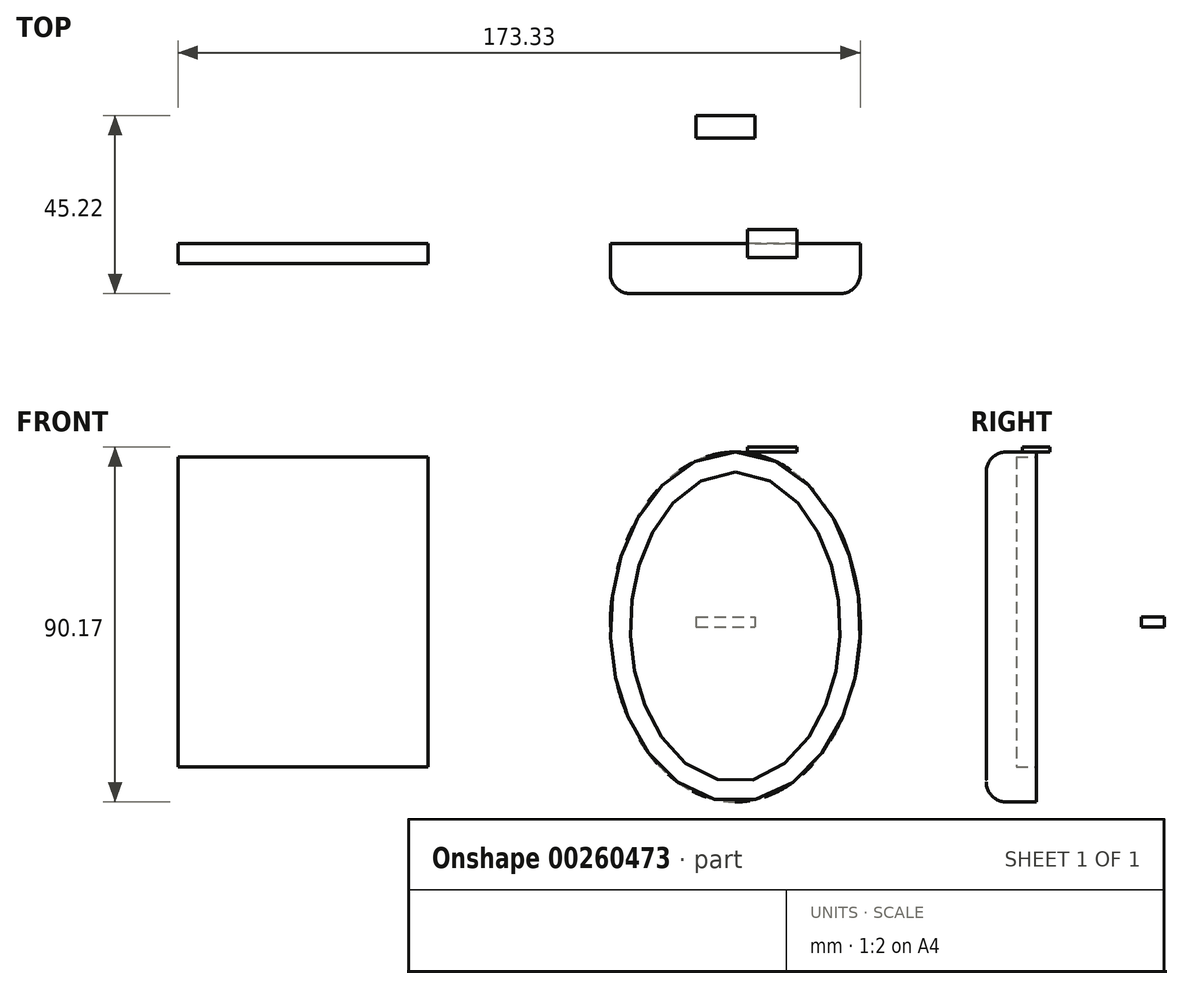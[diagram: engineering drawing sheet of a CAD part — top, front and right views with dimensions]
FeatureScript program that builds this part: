
annotation { "Feature Type Name" : "Feature", "Feature Type Description" : "" }
export const myFeature = defineFeature(function(context is Context, id is Id, definition is map)
    precondition{}
    {
        {
            var Q0;
            Q0=qCreatedBy(makeId("Front.planeOp"),FACE);
            var sketch = newSketch(context, id + "F0", { "sketchPlane" : qUnion([Q0])});
            skEllipse(sketch, "E0", {"center": v(0, 0) * mm, "majorRadius": 31.75 * mm, "minorRadius": 44.45 * mm, "majorAxis": v(1, 0)});
            skSolve(sketch);
        }
        {
            var Q0;
            Q0=makeQuery(id+"F0.imprint","IMPRINT",FACE,{"disambiguationData":[TD([[makeQuery(id+"F0.imprint","IMPRINT",EDGE,{"derivedFrom":sQuery(id+"F0.wireOp",EDGE,"E0")}),1.0]])]});
            extrude(context, id + "F1", {"entities" : qUnion([Q0]), "depth" : 12.7 * mm});
        }
        {
            var Q0;
            Q0=makeQuery(id+"F1.opExtrude","CAP_FACE",FACE,{"disambiguationData":[OSD([sQuery(id+"F0.wireOp",EDGE,"E0")])],"isStart":false});
            fillet(context, id + "F2", {"entities" : qUnion([Q0]), "radius" : 5.08 * mm, "tangentPropagation" : true, "allowEdgeOverflow" : false});
        }
        {
            var Q0;
            Q0=qCreatedBy(makeId("Front.planeOp"),FACE);
            var sketch = newSketch(context, id + "F3", { "sketchPlane" : qUnion([Q0])});
            skLineSegment(sketch, "E1.bottom", {"start": v(-141.58, 43.19) * mm, "end": v(-78.08, 43.19) * mm});
            skLineSegment(sketch, "E1.top", {"start": v(-141.58, -35.55) * mm, "end": v(-78.08, -35.55) * mm});
            skLineSegment(sketch, "E1.left", {"start": v(-141.58, 43.19) * mm, "end": v(-141.58, -35.55) * mm});
            skLineSegment(sketch, "E1.right", {"start": v(-78.08, 43.19) * mm, "end": v(-78.08, -35.55) * mm});
            skPoint(sketch, "E1.middle", {"position": v(-109.83, 3.82) * mm});
            skSolve(sketch);
        }
        {
            var Q0;
            Q0=makeQuery(id+"F3.imprint","IMPRINT",FACE,{"disambiguationData":[TD([[makeQuery(id+"F3.imprint","IMPRINT",EDGE,{"derivedFrom":sQuery(id+"F3.wireOp",EDGE,"E1.bottom")}),-1.0]])]});
            extrude(context, id + "F4", {"entities" : qUnion([Q0]), "depth" : 5.08 * mm});
        }
        {
            var Q0;
            Q0=qCreatedBy(makeId("Top.planeOp"),FACE);
            var sketch = newSketch(context, id + "F5", { "sketchPlane" : qUnion([Q0])});
            skLineSegment(sketch, "E2.bottom", {"start": v(-9.93, 32.52) * mm, "end": v(4.97, 32.52) * mm});
            skLineSegment(sketch, "E2.top", {"start": v(-9.93, 26.74) * mm, "end": v(4.97, 26.74) * mm});
            skLineSegment(sketch, "E2.left", {"start": v(-9.93, 32.52) * mm, "end": v(-9.93, 26.74) * mm});
            skLineSegment(sketch, "E2.right", {"start": v(4.97, 32.52) * mm, "end": v(4.97, 26.74) * mm});
            skSolve(sketch);
        }
        {
            var Q0;
            Q0=makeQuery(id+"F5.imprint","IMPRINT",FACE,{"disambiguationData":[TD([[makeQuery(id+"F5.imprint","IMPRINT",EDGE,{"derivedFrom":sQuery(id+"F5.wireOp",EDGE,"E2.bottom")}),-1.0]])]});
            extrude(context, id + "F6", {"entities" : qUnion([Q0]), "depth" : 2.54 * mm});
        }
        {
            var Q0;
            Q0=qCreatedBy(makeId("Top.planeOp"),FACE);
            cPlane(context, id + "F7", {"entities" : qUnion([Q0]), "cplaneType" : CPlaneType.OFFSET, "offset" : 44.45 * mm, "width" : 152.4 * mm, "height" : 152.4 * mm});
        }
        {
            var Q0;
            Q0=qCreatedBy(id+"F7.planeOp",FACE);
            var sketch = newSketch(context, id + "F8", { "sketchPlane" : qUnion([Q0])});
            skLineSegment(sketch, "E3.bottom", {"start": v(3.05, -3.5) * mm, "end": v(15.7, -3.5) * mm});
            skLineSegment(sketch, "E3.top", {"start": v(3.05, 3.5) * mm, "end": v(15.7, 3.5) * mm});
            skLineSegment(sketch, "E3.left", {"start": v(3.05, -3.5) * mm, "end": v(3.05, 3.5) * mm});
            skLineSegment(sketch, "E3.right", {"start": v(15.7, -3.5) * mm, "end": v(15.7, 3.5) * mm});
            skPoint(sketch, "E3.middle", {"position": v(9.37, 0) * mm});
            skSolve(sketch);
        }
        {
            var Q0;
            Q0=makeQuery(id+"F8.imprint","IMPRINT",FACE,{"disambiguationData":[TD([[makeQuery(id+"F8.imprint","IMPRINT",EDGE,{"derivedFrom":sQuery(id+"F8.wireOp",EDGE,"E3.bottom")}),1.0]])]});
            extrude(context, id + "F9", {"entities" : qUnion([Q0]), "depth" : 1.27 * mm});
        }
    });
